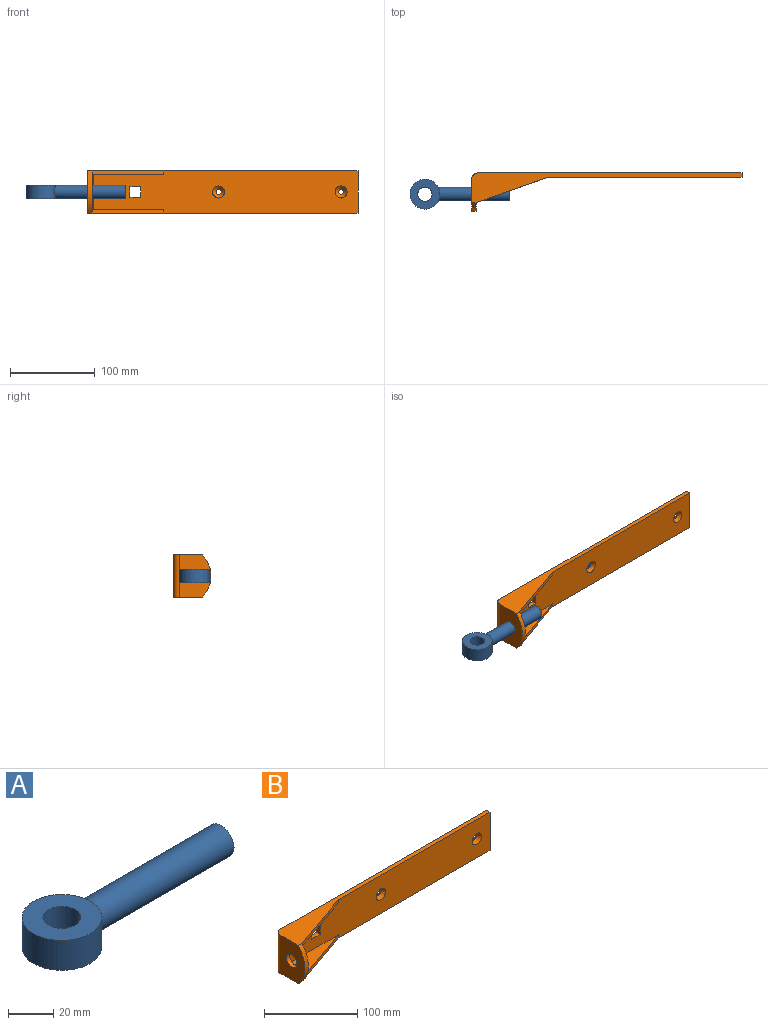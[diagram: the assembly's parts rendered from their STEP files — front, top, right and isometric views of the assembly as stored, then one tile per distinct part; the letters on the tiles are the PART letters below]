
ASSEMBLY  parts=2 mates=2
PART A: 6 faces, bbox 117.7x35.4x16.2 mm
  f0: cylinder r=17.7mm len=35.4mm, axis (0,0,-1), area 1595.1mm2, adj f2,f3,f4
  f1: cylinder r=8.4mm len=16.8mm, axis (0,0,-1), area 855mm2, adj f2,f3
  f2: plane 35.4x35.4mm, normal (0,0,1), area 762.6mm2, adj f0,f1
  f3: plane 35.4x35.4mm, normal (0,0,-1), area 762.6mm2, adj f0,f1
  f4: cylinder r=8mm len=84.21mm, axis (-1,0,0), area 4184.2mm2, adj f0,f5
  f5: plane 16x16mm, normal (1,0,0), area 201.1mm2, adj f4
PART B: 23 faces, bbox 320x45x50 mm
  f0: plane 312.8x50mm, normal (0,-1,0), area 14493.2mm2, adj f4,f5,f6,f8,f10,f11,f12,f13
  f1: plane 312.8x50mm, normal (0,1,0), area 15414.8mm2, adj f2,f5,f6,f8,f9,f15,f17,f18
  f2: cylinder r=3.12mm len=6.25mm, axis (0,1,0), area 23.6mm2, adj f1,f21
  f3: plane 50x37.8mm, normal (1,0,0), area 1310.3mm2, adj f4,f10,f11,f12,f13,f14,f16
  f4: cylinder r=2mm len=42mm, axis (0,0,1), area 131.9mm2, adj f0,f3,f11,f13
  f5: plane 320x35mm, normal (0,0,-1), area 3074.3mm2, adj f0,f1,f7,f8,f9,f12,f14
  f6: plane 320x35mm, normal (0,0,1), area 3074.3mm2, adj f0,f1,f7,f8,f9,f10,f14
  f7: plane 50x37.8mm, normal (-1,0,0), area 1532.7mm2, adj f5,f6,f9,f14,f16
  f8: plane 50x5.2mm, normal (1,0,0), area 260mm2, adj f0,f1,f5,f6
  f9: cylinder r=7.2mm len=50mm, axis (0,0,1), area 565.5mm2, adj f1,f5,f6,f7
  f10: plane 85x29.8mm, normal (0.33,-0.94,0), area 360.3mm2, adj f0,f3,f6,f11
  f11: plane 85x29.8mm, normal (0,0,-1), area 1265.6mm2, adj f0,f3,f4,f10
  f12: plane 85x29.8mm, normal (0.33,-0.94,0), area 360.3mm2, adj f0,f3,f5,f13
  f13: plane 85x29.8mm, normal (0,0,1), area 1265.6mm2, adj f0,f3,f4,f12
  f14: cylinder r=36.25mm len=50mm, axis (-1,0,0), area 286.9mm2, adj f3,f5,f6,f7
  f15: cylinder r=3.12mm len=6.25mm, axis (0,1,0), area 23.6mm2, adj f1,f22
  f16: cylinder r=8mm len=16mm, axis (-1,0,0), area 261.4mm2, adj f3,f7
  f17: plane 12.8x5.2mm, normal (0,0,-1), area 66.6mm2, adj f0,f1,f18,f20
  f18: plane 12.8x5.2mm, normal (-1,0,0), area 66.6mm2, adj f0,f1,f17,f19
  f19: plane 12.8x5.2mm, normal (0,0,1), area 66.6mm2, adj f0,f1,f18,f20
  f20: plane 12.8x5.2mm, normal (1,0,0), area 66.6mm2, adj f0,f1,f17,f19
  f21: cone r=7.12mm half-angle=45deg, axis (0,-1,0), area 182.2mm2, adj f0,f2
  f22: cone r=7.12mm half-angle=45deg, axis (0,-1,0), area 182.2mm2, adj f0,f15
PLACE A t=(-73.51,79.2,-30.35)mm
PLACE B t=(-51.76,79.2,-30.35)mm
MATE slider A.f4 <-> B.f16  axis (-1,0,0) through (7.67,79.2,-29.15)mm
MATE fastened B.f16 <-> A.f4  axis (-1,0,0) through (5.3,79.2,-29.15)mm
